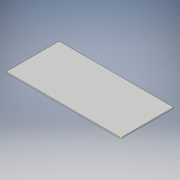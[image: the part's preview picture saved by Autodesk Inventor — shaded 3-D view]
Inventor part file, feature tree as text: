
AUTODESK INVENTOR PART (.ipt)
format: ipt  version: 2017 (Build 210142000, 142)  size: 91,648 bytes
history: native  units: in
note: dims shown in document units (in); Inventor stores cm internally (conversion verified against a paired STEP export)
features: sketch x2, extrude x1
ambient origin geometry x8: Origin, YZ Plane, XZ Plane, XY Plane, X Axis, Y Axis, Z Axis, Center Point
bodies: Solid1 (feature_tree)
feature tree (3):
  extrude  "Extrusion1"  Depth=6.0in
  sketch  "Sketch2"  dims[d2=0.125in d3=0.0in]
  sketch  "Sketch1"  dims[d0=13.0in d1=6.0in]
